# Revit family: QPLE
name_source: partatom
category: Mechanical Equipment
revit_build: Autodesk Revit 2016 (Build: 20150714_1515(x64)
units: mm (PartAtom-declared; Revit-internal decimal feet)

## family parameters
Always vertical = Yes
Cut with Voids When Loaded = No
Part Type = Normal
Room Calculation Point = No
Round Connector Dimension = Use Radius
Shared = No
Work Plane-Based = No

## types (4) — shared parameters
Description = Lo-Profile Parallel Fan Powered Air Terminal with Electric Reheat
Discharge Height "Y" = 9"
Discharge Width "X" = 11 1/2"
Height = 10 1/2"
Induction Width "C" = 16"
Length = 34"
Manufacturer = Anemostat
Model = QPLE
URL = http://www.anemostat.com
Width = 32"

## per-type parameters (varying)
| type | Diameter | Duct Inlet Radius | Radius |
| QPLE - 5" Inlet (ERC) | 4 7/8" | 2" | 2 7/16" |
| QPLE - 6" Inlet (ERC) | 5 7/8" | 3" | 2 15/16" |
| QPLE - 7" Inlet (ERC) | 6 7/8" | 3" | 3 7/16" |
| QPLE - 8" Inlet (ERC) | 7 7/8" | 4" | 3 15/16" |

## geometry (parser evidence)
native form markers: Sweep x2
no freeform markers — native parametric forms only
